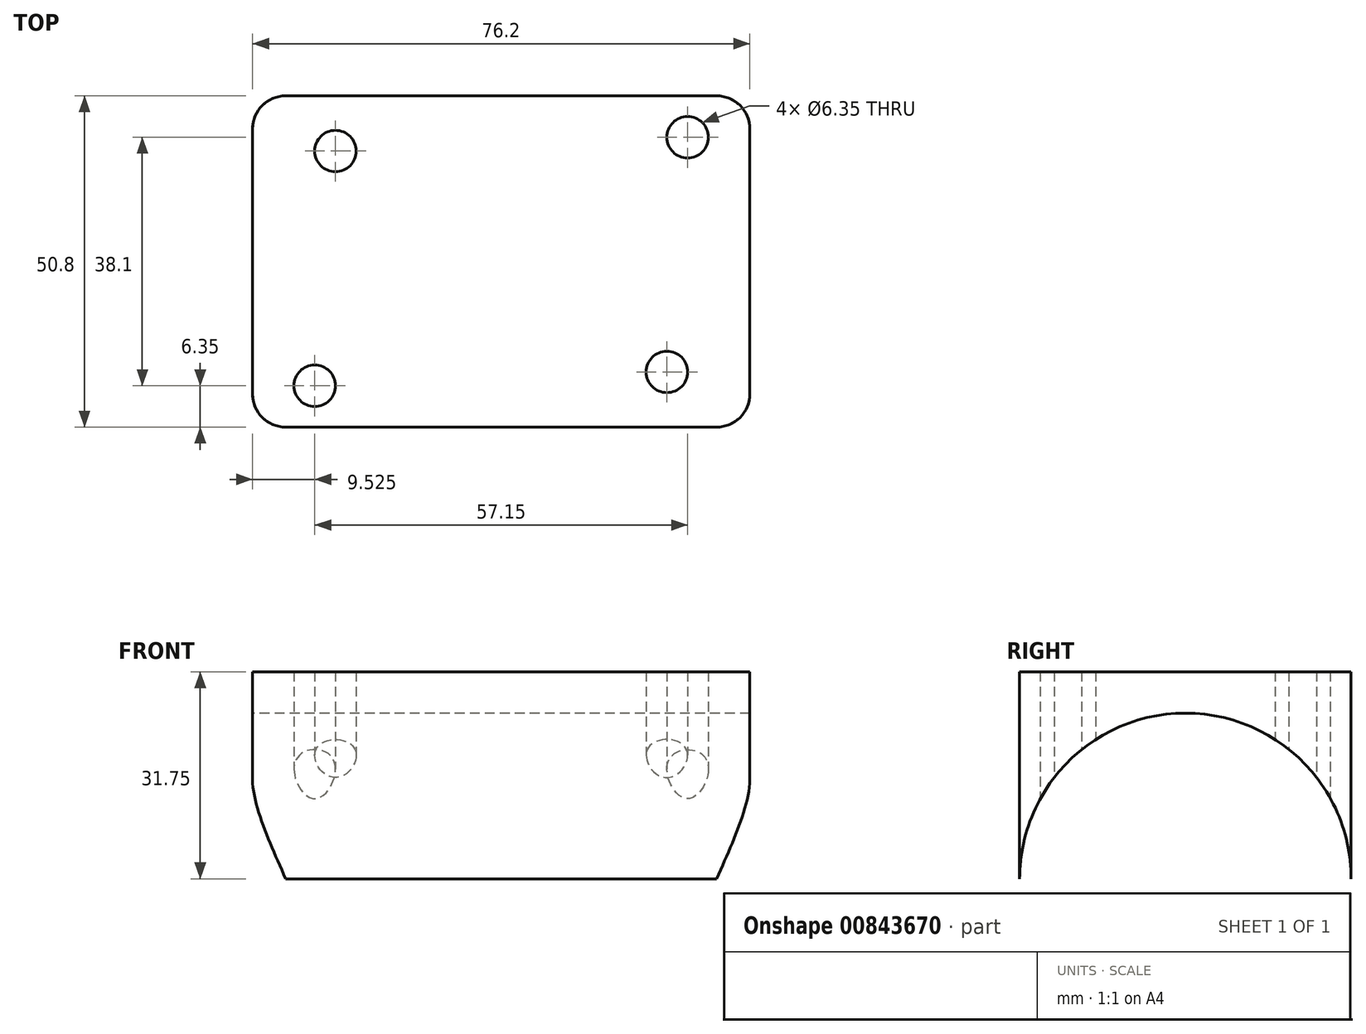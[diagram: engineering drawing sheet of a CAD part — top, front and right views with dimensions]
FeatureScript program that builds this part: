
annotation { "Feature Type Name" : "Feature", "Feature Type Description" : "" }
export const myFeature = defineFeature(function(context is Context, id is Id, definition is map)
    precondition{}
    {
        {
            var Q0;
            Q0=qCreatedBy(makeId("Top.planeOp"),FACE);
            var sketch = newSketch(context, id + "F0", { "sketchPlane" : qUnion([Q0])});
            skLineSegment(sketch, "E0.bottom", {"start": v(38.1, 25.4) * mm, "end": v(-38.1, 25.4) * mm});
            skLineSegment(sketch, "E0.top", {"start": v(38.1, -25.4) * mm, "end": v(-38.1, -25.4) * mm});
            skLineSegment(sketch, "E0.left", {"start": v(38.1, 25.4) * mm, "end": v(38.1, -25.4) * mm});
            skLineSegment(sketch, "E0.right", {"start": v(-38.1, 25.4) * mm, "end": v(-38.1, -25.4) * mm});
            skPoint(sketch, "E0.middle", {"position": v(0, 0) * mm});
            skLineSegment(sketch, "E1", {"start": v(-38.1, 25.4) * mm, "end": v(38.1, -25.4) * mm, "construction": true});
            skLineSegment(sketch, "E2", {"start": v(-38.1, -25.4) * mm, "end": v(38.1, 25.4) * mm, "construction": true});
            skCircle(sketch, "E3", {"center": v(-25.4, 16.93) * mm, "radius": 3.18 * mm});
            skCircle(sketch, "E4", {"center": v(28.57, 19.05) * mm, "radius": 3.18 * mm});
            skCircle(sketch, "E5", {"center": v(-28.57, -19.05) * mm, "radius": 3.18 * mm});
            skCircle(sketch, "E6", {"center": v(25.4, -16.93) * mm, "radius": 3.18 * mm});
            skSolve(sketch);
        }
        {
            var Q0;
            Q0 = qSketchRegion(id + "F0", true);
            extrude(context, id + "F1", {"entities" : qUnion([Q0]), "depth" : 31.75 * mm, "offsetDistance" : 25.4 * mm});
        }
        {
            var Q0;
            Q0=makeQuery(id+"F1.opExtrude","SWEPT_EDGE",EDGE,{"disambiguationData":[OSD([sQuery(id+"F0.wireOp",EDGE,"E0.bottom"),sQuery(id+"F0.wireOp",EDGE,"E0.right")])]});
            var Q1;
            Q1=makeQuery(id+"F1.opExtrude","SWEPT_EDGE",EDGE,{"disambiguationData":[OSD([sQuery(id+"F0.wireOp",EDGE,"E0.top"),sQuery(id+"F0.wireOp",EDGE,"E0.right")])]});
            var Q2;
            Q2=makeQuery(id+"F1.opExtrude","SWEPT_EDGE",EDGE,{"disambiguationData":[OSD([sQuery(id+"F0.wireOp",EDGE,"E0.bottom"),sQuery(id+"F0.wireOp",EDGE,"E0.left")])]});
            var Q3;
            Q3=makeQuery(id+"F1.opExtrude","SWEPT_EDGE",EDGE,{"disambiguationData":[OSD([sQuery(id+"F0.wireOp",EDGE,"E0.top"),sQuery(id+"F0.wireOp",EDGE,"E0.left")])]});
            fillet(context, id + "F2", {"entities" : qUnion([Q0, Q1, Q2, Q3]), "radius" : 5.08 * mm, "tangentPropagation" : true, "allowEdgeOverflow" : false});
        }
        {
            var Q0;
            Q0=makeQuery(id+"F1.opExtrude","SWEPT_FACE",FACE,{"disambiguationData":[OSD([sQuery(id+"F0.wireOp",EDGE,"E0.right")])]});
            var sketch = newSketch(context, id + "F3", { "sketchPlane" : qUnion([Q0])});
            skArc(sketch, "E7", {"start": v(25.4, 0) * mm, "mid": v(0, 25.4) * mm, "end": v(-25.4, 0) * mm});
            skLineSegment(sketch, "E8", {"start": v(-25.4, 0) * mm, "end": v(25.4, 0) * mm});
            skSolve(sketch);
        }
        {
            var Q0;
            Q0 = qSketchRegion(id + "F3", true);
            extrude(context, id + "F4", {"entities" : qUnion([Q0]), "operationType" : NewBodyOperationType.REMOVE, "endBound" : BoundingType.THROUGH_ALL, "oppositeDirection" : true, "depth" : 25.4 * mm, "offsetDistance" : 25.4 * mm});
        }
    });
